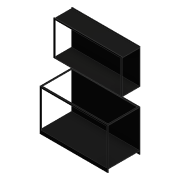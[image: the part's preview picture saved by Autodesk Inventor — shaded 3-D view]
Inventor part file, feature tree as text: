
AUTODESK INVENTOR PART (.ipt)
format: ipt  version: 2016 (Build 200138000, 138)  size: 250,368 bytes
history: native  units: mm
features: extrude x9, projected_geometry x9, sketch x8, plane x1
ambient origin geometry x8: Origin, YZ Plane, XZ Plane, XY Plane, X Axis, Y Axis, Z Axis, Center Point
bodies: Solid1 (feature_tree)
feature tree (27):
  extrude  "Extrusion1"  Depth=10.0mm
  extrude  "Extrusion2"  Depth=80.0mm
  extrude  "Extrusion3"  Depth=30.0mm
  extrude  "Extrusion4"  Depth=30.0mm
  plane  "Work Plane1"
  extrude  "Extrusion5"  Depth=10.0mm
  extrude  "Extrusion9"  Depth=10.0mm
  extrude  "Extrusión10"  Depth=30.0mm
  extrude  "Extrusión11"  TaperAngle=0.0deg  [1 undecoded]
  extrude  "Extrusion13"  Depth=2033.333333mm
  sketch  "Sketch1"  dims[d3=0.0mm d5=10.0mm]
  sketch  "Sketch2"  dims[d6=10.0mm d7=80.0mm]
  projected_geometry  "Projected Loop1"
  sketch  "Sketch3"  dims[d9=0.0mm d10=30.0mm]
  projected_geometry  "Projected Loop2"
  sketch  "Sketch4"  dims[d11=400.0mm d12=0.0mm d13=30.0mm]
  projected_geometry  "Projected Loop3"
  projected_geometry  "Projected Loop4"
  projected_geometry  "Projected Loop5"
  sketch  "Sketch5"  dims[d14=30.0mm d15=10.0mm]
  sketch  "Sketch9"  dims[d16=0.0mm d18=10.0mm]
  projected_geometry  "Projected Loop9"
  sketch  "Boceto10"  dims[d19=0.0mm d32=30.0mm]
  projected_geometry  "Contorno proyectado10"
  projected_geometry  "Contorno proyectado11"
  sketch  "Sketch13"  dims[d33=10.0mm d34=0.0mm d36=2033.333333mm d39=10.0mm d40=10.0mm d41=10.0mm d43=0.0mm d44=30.0mm d45=30.0mm d46=30.0mm d48=750.0mm d49=0.0mm d53=10.0mm d54=20.0mm d55=2033.333333mm d56=0.0mm]
  projected_geometry  "Projected Loop12"
note: 1 required parameter value undecoded (feature->parameter linkage not recoverable at this tier; creation-order binding heuristic only, values carry confidence <= 0.55)
